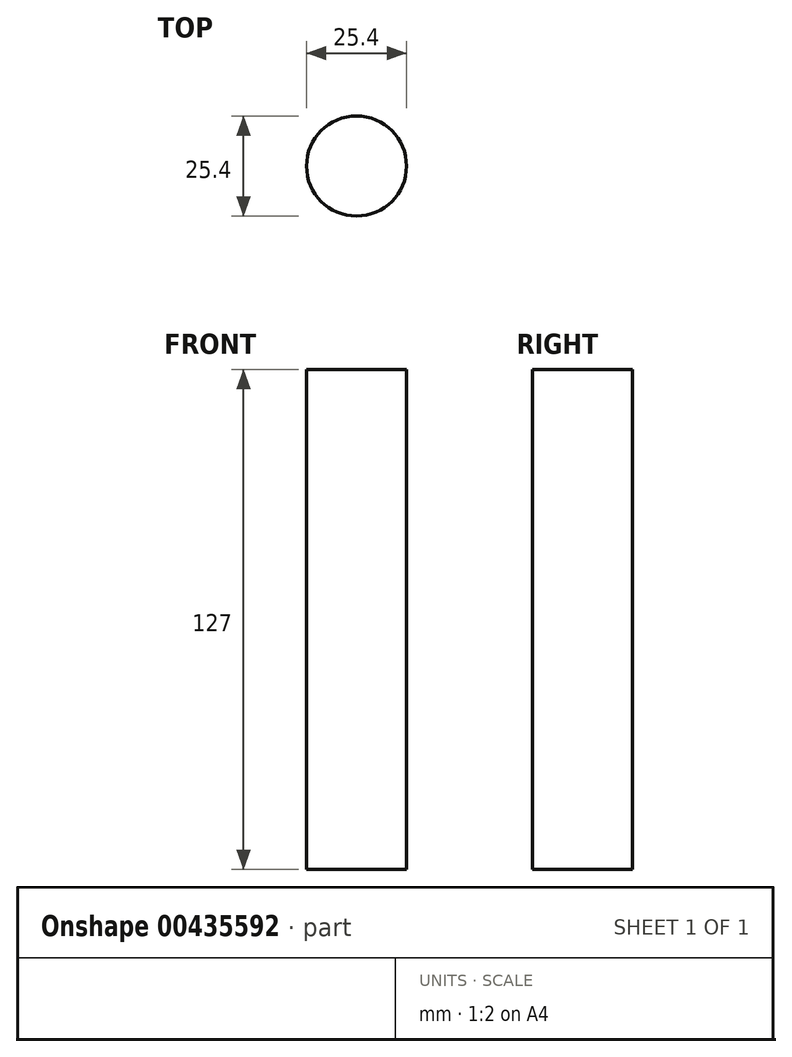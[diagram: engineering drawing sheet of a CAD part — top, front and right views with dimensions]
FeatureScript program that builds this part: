
annotation { "Feature Type Name" : "Feature", "Feature Type Description" : "" }
export const myFeature = defineFeature(function(context is Context, id is Id, definition is map)
    precondition{}
    {
        {
            var Q0;
            Q0=qCreatedBy(makeId("Top.planeOp"),FACE);
            var sketch = newSketch(context, id + "F0", { "sketchPlane" : qUnion([Q0])});
            skCircle(sketch, "E0", {"center": v(0, 0) * mm, "radius": 12.7 * mm});
            skSolve(sketch);
        }
        {
            var Q0;
            Q0 = qSketchRegion(id + "F0", true);
            extrude(context, id + "F1", {"entities" : qUnion([Q0]), "endBound" : BoundingType.SYMMETRIC, "oppositeDirection" : true, "depth" : 127 * mm});
        }
    });
